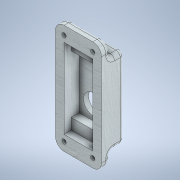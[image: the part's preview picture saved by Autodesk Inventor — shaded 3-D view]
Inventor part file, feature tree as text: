
AUTODESK INVENTOR PART (.ipt)
format: ipt  version: 2021 (Build 250183000, 183)  size: 275,968 bytes
history: native  units: mm
features: extrude x7, sketch x7, fillet x3
ambient origin geometry x8: Origin, YZ Plane, XZ Plane, XY Plane, X Axis, Y Axis, Z Axis, Center Point
bodies: Solid1 (feature_tree)
feature tree (17):
  extrude  "Extrusion1"  Depth=76.0mm
  fillet  "Fillet1"  Radius=16.0mm
  extrude  "Extrusion2"  Depth=20.0mm
  extrude  "Extrusion3"  Depth=18.0mm
  extrude  "Extrusion4"  Depth=10.5mm TaperAngle=0.0deg
  extrude  "Extrusion5"  Depth=10.0mm
  fillet  "Fillet2"  Radius=10.0mm
  extrude  "Extrusion6"  Depth=7.7mm
  extrude  "Extrusion7"  Depth=2.0mm
  fillet  "Fillet3"  Radius=5.0mm
  sketch  "Sketch1"  dims[d0=32.0mm d1=76.0mm d2=16.0mm d3=0.0mm]
  sketch  "Sketch2"  dims[d4=6.0mm d5=20.0mm]
  sketch  "Sketch3"  dims[d6=40.0mm d7=18.0mm]
  sketch  "Sketch4"  dims[d8=6.0mm d9=10.5mm d10=0.0mm]
  sketch  "Sketch5"  dims[d11=14.0mm d12=10.0mm d13=10.0mm]
  sketch  "Sketch6"  dims[d14=12.5mm d15=0.0mm d16=7.7mm]
  sketch  "Sketch7"  dims[d17=20.0mm d18=7.7mm d19=5.0mm d20=0.0mm d21=10.0mm d22=10.0mm d23=10.0mm d24=10.0mm d25=5.0mm d26=0.0mm d27=3.0mm d28=3.0mm d29=3.0mm d30=3.0mm d31=3.0mm d32=5.0mm d33=10.0mm d34=0.0mm d35=0.0mm d36=22.0mm d37=2.0mm d38=0.0mm d39=2.0mm]
